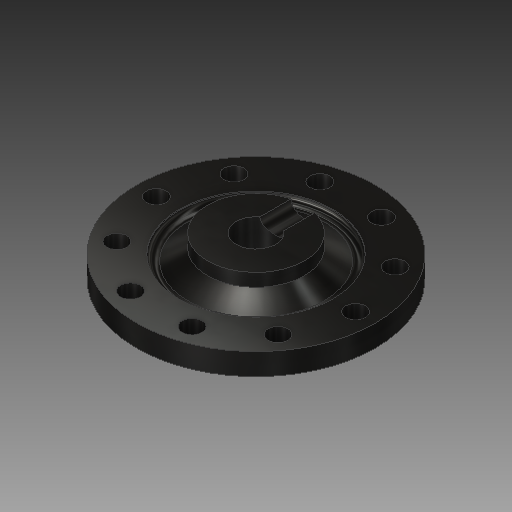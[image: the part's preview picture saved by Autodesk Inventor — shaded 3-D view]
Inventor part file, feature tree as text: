
AUTODESK INVENTOR PART (.ipt)
format: ipt  version: 2019 (Build 230136000, 136)  size: 207,360 bytes
history: native  units: mm
features: sketch x4, hole x3, revolve x1, fillet x1, pattern_circular x1
ambient origin geometry x8: Origin, YZ Plane, XZ Plane, XY Plane, X Axis, Y Axis, Z Axis, Center Point
bodies: Solid1 (feature_tree)
feature tree (10):
  revolve  "Revolution1"  [1 undecoded]
  fillet  "Fillet1"  Radius=5.439mm
  hole  "Hole1"  [1 undecoded]
  pattern_circular  "Circular Pattern1"  Angle=90.0deg  [1 undecoded]
  hole  "Hole2"  [1 undecoded]
  hole  "Hole3"  [1 undecoded]
  sketch  "Sketch1"  dims[d1=30.0mm d2=10.043mm d3=5.439mm]
  sketch  "Sketch2"  dims[d4=10.608mm d5=3.231mm]
  sketch  "Sketch3"  dims[d6=21.048671mm]
  sketch  "Sketch4"  dims[d7=17.845mm d8=90.0deg d9=1.5mm d10=25.0mm d11=5.0mm d12=6.0mm d13=4.0mm d14=2.0mm d15=90.0deg d16=8.0mm d17=20.594885mm d18=100.0mm d19=360.0deg d21=7.936mm d22=6.0mm d23=9.938mm d24=7.672mm d25=90.0deg d26=8.0mm d27=20.594885mm d28=6.0mm d29=6.0mm d30=9.938mm d31=2.0mm d32=90.0deg d33=8.0mm d34=20.594885mm]
note: 5 required parameter values undecoded (feature->parameter linkage not recoverable at this tier; creation-order binding heuristic only, values carry confidence <= 0.55)